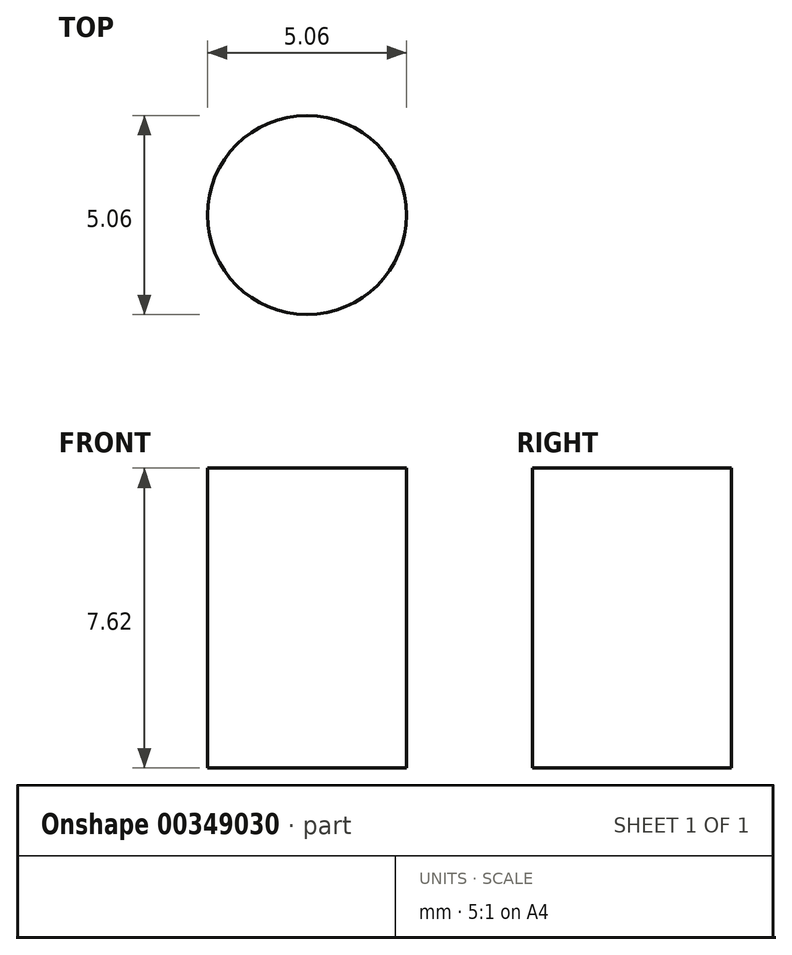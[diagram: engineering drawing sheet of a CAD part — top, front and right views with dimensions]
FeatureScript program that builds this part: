
annotation { "Feature Type Name" : "Feature", "Feature Type Description" : "" }
export const myFeature = defineFeature(function(context is Context, id is Id, definition is map)
    precondition{}
    {
        {
            var Q0;
            Q0=qCreatedBy(makeId("Top.planeOp"),FACE);
            var sketch = newSketch(context, id + "F0", { "sketchPlane" : qUnion([Q0])});
            skCircle(sketch, "E0", {"center": v(0, 0) * mm, "radius": 2.53 * mm});
            skSolve(sketch);
        }
        {
            var Q0;
            Q0=makeQuery(id+"F0.imprint","IMPRINT",FACE,{"disambiguationData":[TD([[makeQuery(id+"F0.imprint","IMPRINT",EDGE,{"derivedFrom":sQuery(id+"F0.wireOp",EDGE,"E0")}),1.0]])]});
            extrude(context, id + "F1", {"entities" : qUnion([Q0]), "depth" : 7.62 * mm});
        }
    });
